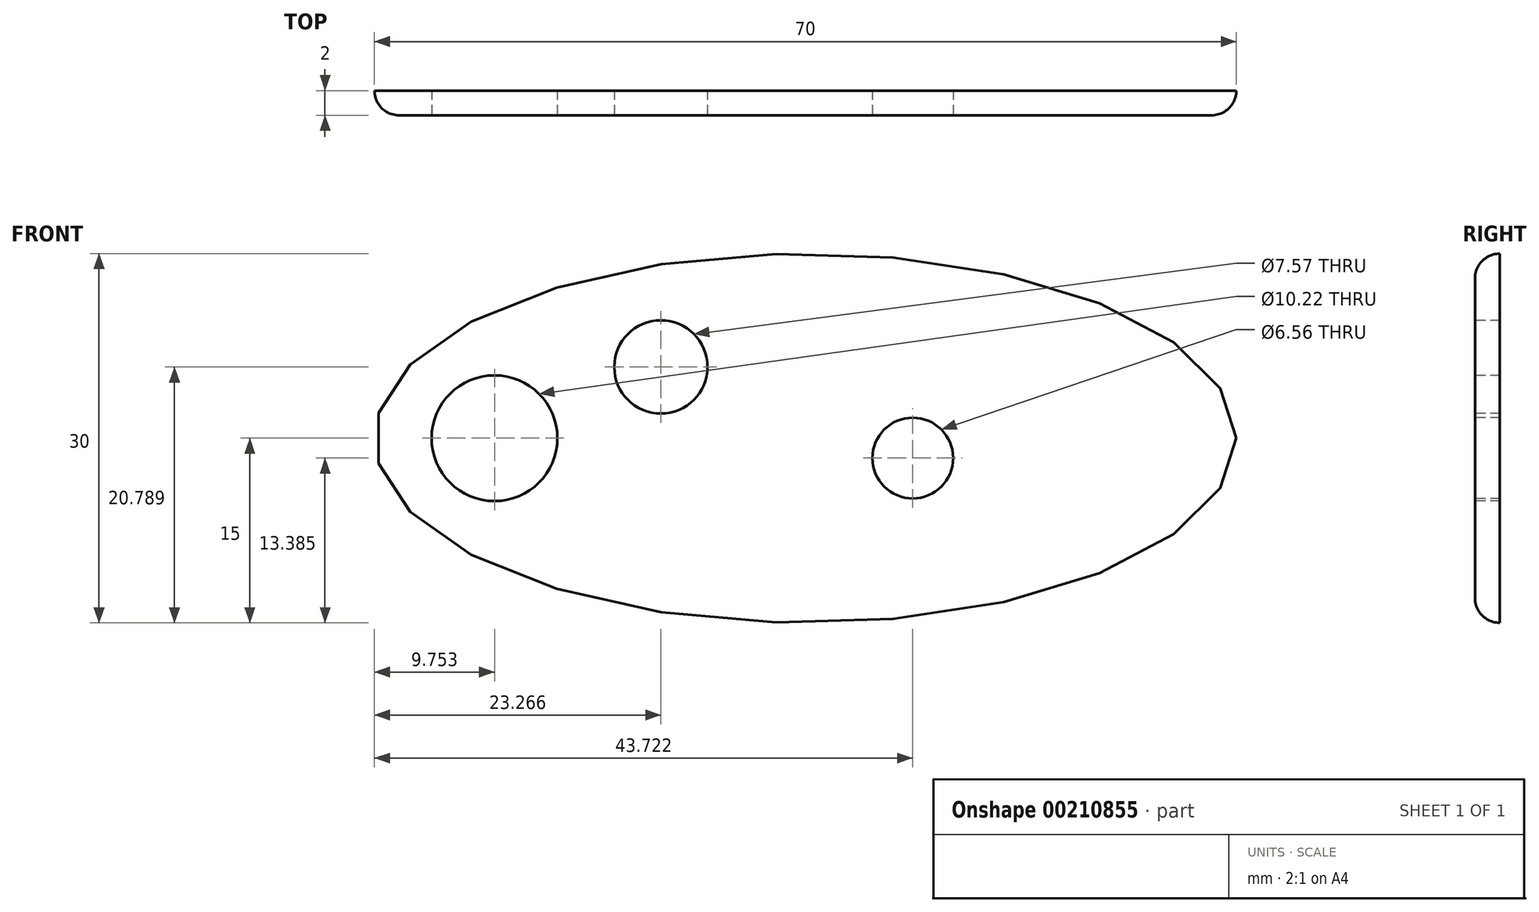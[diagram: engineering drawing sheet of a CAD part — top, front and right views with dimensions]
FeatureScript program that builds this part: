
annotation { "Feature Type Name" : "Feature", "Feature Type Description" : "" }
export const myFeature = defineFeature(function(context is Context, id is Id, definition is map)
    precondition{}
    {
        {
            var Q0;
            Q0=qCreatedBy(makeId("Front.planeOp"),FACE);
            var sketch = newSketch(context, id + "F0", { "sketchPlane" : qUnion([Q0])});
            skEllipse(sketch, "E0", {"center": v(0, 0) * mm, "majorRadius": 35 * mm, "minorRadius": 15 * mm, "majorAxis": v(1, 0)});
            skSolve(sketch);
        }
        {
            var Q0;
            Q0 = qSketchRegion(id + "F0", true);
            extrude(context, id + "F1", {"entities" : qUnion([Q0]), "depth" : 2 * mm});
        }
        {
            var Q0;
            Q0=makeQuery(id+"F1.opExtrude","CAP_FACE",FACE,{"disambiguationData":[OSD([sQuery(id+"F0.wireOp",EDGE,"E0")])],"isStart":false});
            var sketch = newSketch(context, id + "F2", { "sketchPlane" : qUnion([Q0])});
            skCircle(sketch, "E1", {"center": v(-11.73, 5.79) * mm, "radius": 3.79 * mm});
            skSolve(sketch);
        }
        {
            var Q0;
            Q0 = qSketchRegion(id + "F2", true);
            extrude(context, id + "F3", {"entities" : qUnion([Q0]), "operationType" : NewBodyOperationType.REMOVE, "oppositeDirection" : true, "depth" : 25 * mm});
        }
        {
            var Q0;
            Q0=makeQuery(id+"F1.opExtrude","CAP_FACE",FACE,{"disambiguationData":[OSD([sQuery(id+"F0.wireOp",EDGE,"E0")])],"isStart":false});
            var sketch = newSketch(context, id + "F4", { "sketchPlane" : qUnion([Q0])});
            skCircle(sketch, "E2", {"center": v(-25.25, 0) * mm, "radius": 5.1 * mm});
            skSolve(sketch);
        }
        {
            var Q0;
            Q0 = qSketchRegion(id + "F4", true);
            extrude(context, id + "F5", {"entities" : qUnion([Q0]), "operationType" : NewBodyOperationType.REMOVE, "oppositeDirection" : true, "depth" : 25 * mm});
        }
        {
            var Q0;
            Q0=makeQuery(id+"F1.opExtrude","CAP_FACE",FACE,{"disambiguationData":[OSD([sQuery(id+"F0.wireOp",EDGE,"E0")])],"isStart":false});
            var sketch = newSketch(context, id + "F6", { "sketchPlane" : qUnion([Q0])});
            skCircle(sketch, "E3", {"center": v(8.72, -1.61) * mm, "radius": 3.28 * mm});
            skSolve(sketch);
        }
        {
            var Q0;
            Q0 = qSketchRegion(id + "F6", true);
            extrude(context, id + "F7", {"entities" : qUnion([Q0]), "operationType" : NewBodyOperationType.REMOVE, "oppositeDirection" : true, "depth" : 25 * mm});
        }
        {
            var Q0;
            Q0=makeQuery(id+"F1.opExtrude","CAP_EDGE",EDGE,{"disambiguationData":[OSD([sQuery(id+"F0.wireOp",EDGE,"E0")])],"isStart":false});
            fillet(context, id + "F8", {"entities" : qUnion([Q0]), "radius" : 2 * mm, "tangentPropagation" : true, "allowEdgeOverflow" : false});
        }
    });
